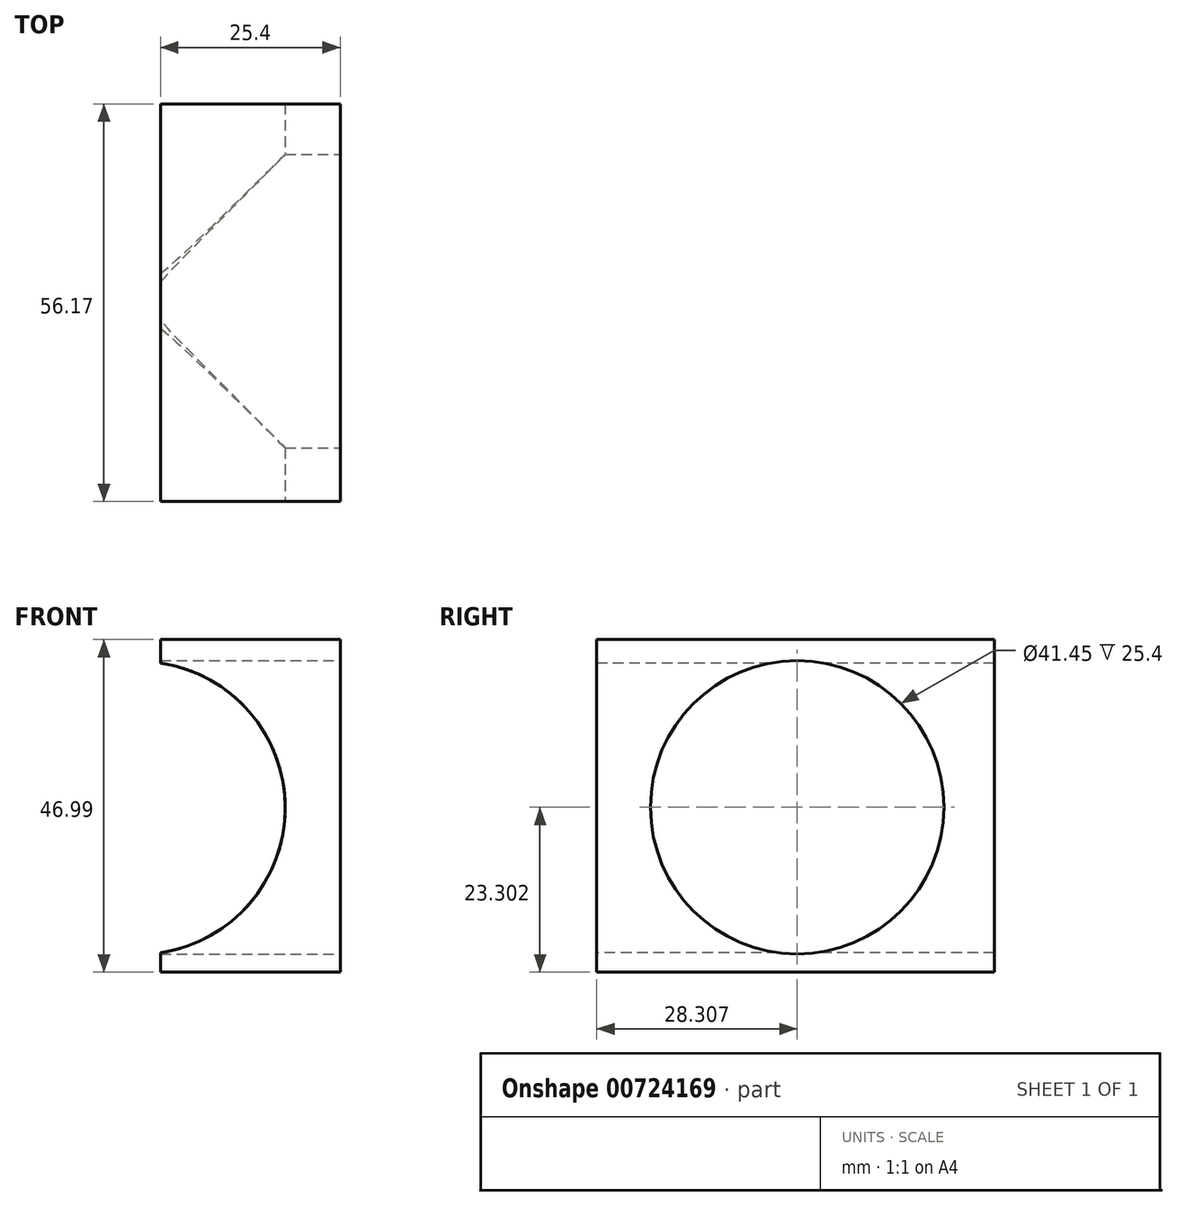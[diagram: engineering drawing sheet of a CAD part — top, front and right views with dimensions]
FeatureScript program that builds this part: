
annotation { "Feature Type Name" : "Feature", "Feature Type Description" : "" }
export const myFeature = defineFeature(function(context is Context, id is Id, definition is map)
    precondition{}
    {
        {
            var Q0;
            Q0=qCreatedBy(makeId("Top.planeOp"),FACE);
            var sketch = newSketch(context, id + "F0", { "sketchPlane" : qUnion([Q0])});
            skLineSegment(sketch, "E0.bottom", {"start": v(35.3, 52.34) * mm, "end": v(-35.3, 52.34) * mm});
            skLineSegment(sketch, "E0.top", {"start": v(35.3, -52.34) * mm, "end": v(-35.3, -52.34) * mm});
            skLineSegment(sketch, "E0.left", {"start": v(35.3, 52.34) * mm, "end": v(35.3, -52.34) * mm});
            skLineSegment(sketch, "E0.right", {"start": v(-35.3, 52.34) * mm, "end": v(-35.3, -52.34) * mm});
            skPoint(sketch, "E0.middle", {"position": v(0, 0) * mm});
            skSolve(sketch);
        }
        {
            var Q0;
            Q0 = qSketchRegion(id + "F0", true);
            extrude(context, id + "F1", {"entities" : qUnion([Q0]), "depth" : 52.07 * mm, "offsetDistance" : 25.4 * mm});
        }
        {
            var Q0;
            Q0=makeQuery(id+"F1.opExtrude","SWEPT_FACE",FACE,{"disambiguationData":[OSD([sQuery(id+"F0.wireOp",EDGE,"E0.top")])]});
            var sketch = newSketch(context, id + "F2", { "sketchPlane" : qUnion([Q0])});
            skCircle(sketch, "E1", {"center": v(-6.36, 23.21) * mm, "radius": 20.69 * mm});
            skSolve(sketch);
        }
        {
            var Q0;
            Q0=makeQuery(id+"F2.imprint","IMPRINT",FACE,{"disambiguationData":[TD([[makeQuery(id+"F2.imprint","IMPRINT",EDGE,{"derivedFrom":sQuery(id+"F2.wireOp",EDGE,"E1")}),1.0]])]});
            extrude(context, id + "F3", {"entities" : qUnion([Q0]), "operationType" : NewBodyOperationType.REMOVE, "oppositeDirection" : true, "depth" : 118.62 * mm, "offsetDistance" : 25.4 * mm});
        }
        {
            var Q0;
            Q0=makeQuery(id+"F1.opExtrude","SWEPT_FACE",FACE,{"disambiguationData":[OSD([sQuery(id+"F0.wireOp",EDGE,"E0.left")])]});
            var sketch = newSketch(context, id + "F4", { "sketchPlane" : qUnion([Q0])});
            skCircle(sketch, "E2", {"center": v(2.89, 23.3) * mm, "radius": 20.73 * mm});
            skSolve(sketch);
        }
        {
            var Q0;
            Q0 = qSketchRegion(id + "F4", true);
            extrude(context, id + "F5", {"entities" : qUnion([Q0]), "operationType" : NewBodyOperationType.REMOVE, "oppositeDirection" : true, "depth" : 93.98 * mm, "offsetDistance" : 25.4 * mm});
        }
        {
            var Q0;
            Q0=makeQuery(id+"F1.opExtrude","SWEPT_FACE",FACE,{"disambiguationData":[OSD([sQuery(id+"F0.wireOp",EDGE,"E0.bottom")])]});
            extrude(context, id + "F6", {"entities" : qUnion([Q0]), "operationType" : NewBodyOperationType.REMOVE, "oppositeDirection" : true, "depth" : 21.59 * mm, "offsetDistance" : 25.4 * mm});
        }
        {
            var Q0;
            Q0=makeQuery(id+"F1.opExtrude","SWEPT_FACE",FACE,{"disambiguationData":[OSD([sQuery(id+"F0.wireOp",EDGE,"E0.top")])]});
            extrude(context, id + "F7", {"entities" : qUnion([Q0]), "operationType" : NewBodyOperationType.REMOVE, "oppositeDirection" : true, "depth" : 26.92 * mm, "offsetDistance" : 25.4 * mm});
        }
        {
            var Q0;
            Q0=makeQuery(id+"F1.opExtrude","SWEPT_FACE",FACE,{"disambiguationData":[OSD([sQuery(id+"F0.wireOp",EDGE,"E0.left")])]});
            extrude(context, id + "F8", {"entities" : qUnion([Q0]), "operationType" : NewBodyOperationType.REMOVE, "oppositeDirection" : true, "depth" : 13.2 * mm, "offsetDistance" : 25.4 * mm});
        }
        {
            var Q0;
            Q0=makeQuery(id+"F1.opExtrude","CAP_FACE",FACE,{"disambiguationData":[OSD([sQuery(id+"F0.wireOp",EDGE,"E0.bottom"),sQuery(id+"F0.wireOp",EDGE,"E0.top"),sQuery(id+"F0.wireOp",EDGE,"E0.left"),sQuery(id+"F0.wireOp",EDGE,"E0.right")])],"isStart":false});
            extrude(context, id + "F9", {"entities" : qUnion([Q0]), "operationType" : NewBodyOperationType.REMOVE, "oppositeDirection" : true, "depth" : 5.08 * mm, "offsetDistance" : 25.4 * mm});
        }
        {
            var Q0;
            Q0=makeQuery(id+"F8.boolean.opBoolean","COPY",FACE,{"derivedFrom":makeQuery(id+"F8.opExtrude","CAP_FACE",FACE,{"disambiguationData":[OSD([sQuery(id+"F0.wireOp",EDGE,"E0.left")])],"isStart":false})});
            extrude(context, id + "F10", {"entities" : qUnion([Q0]), "operationType" : NewBodyOperationType.INTERSECT, "oppositeDirection" : true, "depth" : 25.4 * mm, "offsetDistance" : 25.4 * mm});
        }
    });
